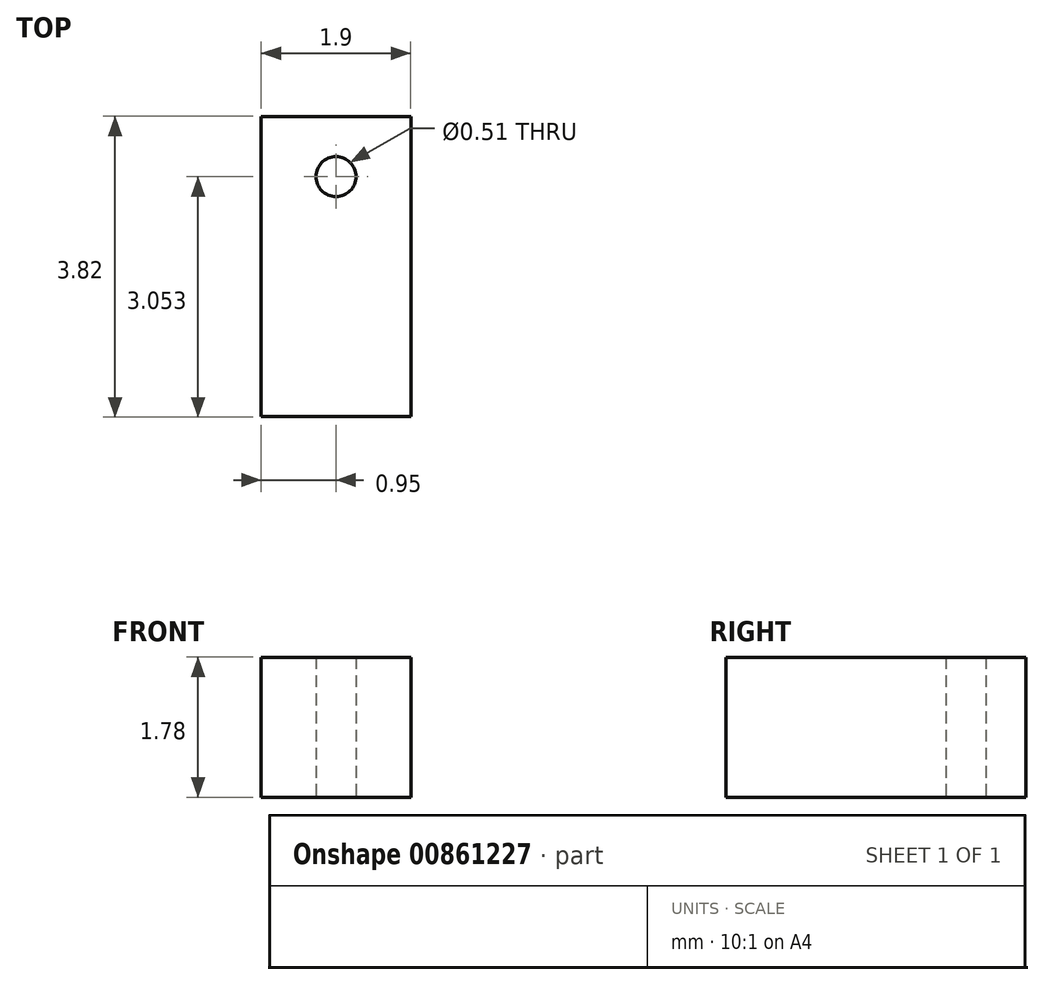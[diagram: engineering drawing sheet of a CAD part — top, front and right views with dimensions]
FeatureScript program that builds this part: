
annotation { "Feature Type Name" : "Feature", "Feature Type Description" : "" }
export const myFeature = defineFeature(function(context is Context, id is Id, definition is map)
    precondition{}
    {
        {
            var Q0;
            Q0=qCreatedBy(makeId("Top.planeOp"),FACE);
            var sketch = newSketch(context, id + "F0", { "sketchPlane" : qUnion([Q0])});
            skLineSegment(sketch, "E0.bottom", {"start": v(0.95, -1.9) * mm, "end": v(-0.95, -1.9) * mm});
            skLineSegment(sketch, "E0.top", {"start": v(0.95, 1.9) * mm, "end": v(-0.95, 1.9) * mm});
            skLineSegment(sketch, "E0.left", {"start": v(0.95, -1.9) * mm, "end": v(0.95, 1.9) * mm});
            skLineSegment(sketch, "E0.right", {"start": v(-0.95, -1.9) * mm, "end": v(-0.95, 1.9) * mm});
            skPoint(sketch, "E0.middle", {"position": v(0, 0) * mm});
            skCircle(sketch, "E1", {"center": v(0, 1.14) * mm, "radius": 0.25 * mm});
            skSolve(sketch);
        }
        {
            var Q0;
            Q0 = qSketchRegion(id + "F0", true);
            extrude(context, id + "F1", {"entities" : qUnion([Q0]), "depth" : 1.78 * mm, "offsetDistance" : 25.4 * mm});
        }
    });
